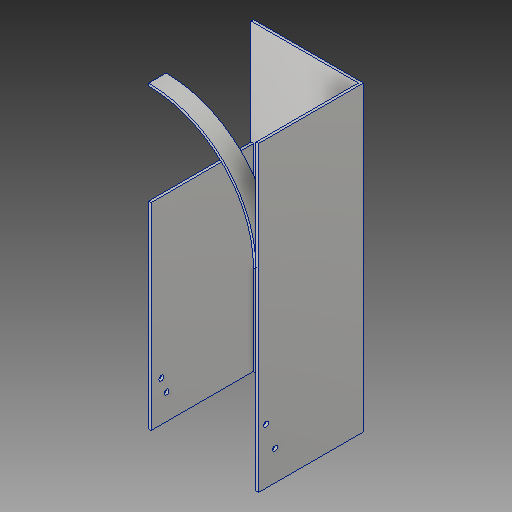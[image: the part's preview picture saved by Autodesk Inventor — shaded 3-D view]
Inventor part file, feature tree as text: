
AUTODESK INVENTOR PART (.ipt)
format: ipt  version: 2019 (Build 230136000, 136)  size: 156,672 bytes
history: native  units: in
note: dims shown in document units (in); Inventor stores cm internally (conversion verified against a paired STEP export)
features: sketch x6, extrude x4, hole x2
ambient origin geometry x8: Origin, YZ Plane, XZ Plane, XY Plane, X Axis, Y Axis, Z Axis, Center Point
bodies: Solid1 (feature_tree)
feature tree (12):
  extrude  "Extrusion1"  Depth=8.646in
  extrude  "Extrusion2"  Depth=0.073in
  extrude  "Extrusion3"  Depth=3.0in
  extrude  "Extrusion7"  Depth=3.0in
  hole  "Hole1"  [1 undecoded]
  hole  "Hole2"  [1 undecoded]
  sketch  "Sketch1"  dims[d0=3.146in d1=8.646in]
  sketch  "Sketch2"  dims[d2=3.0in d3=0.0in d4=0.073in]
  sketch  "Sketch3"  dims[d5=0.073in d6=3.0in]
  sketch  "Sketch9"  dims[d7=9.0in d8=0.0in d9=3.0in]
  sketch  "Sketch10"  dims[d10=2.927in d11=0.0in d22=45.0deg]
  sketch  "Sketch11"  dims[d23=0.073in d24=0.073in d25=0.5in d26=0.0in d27=0.731in d28=0.441in d29=0.289in d30=1.15in d31=0.146in d32=0.38in d33=0.375in d34=0.25in d35=0.5635in d36=0.588in d37=0.8108in d38=1.581in d39=0.213in d40=0.477in d41=0.857in d42=0.146in d43=0.38in d44=0.375in d45=0.25in d46=0.5635in d47=0.588in d48=0.8108in]
note: 2 required parameter values undecoded (feature->parameter linkage not recoverable at this tier; creation-order binding heuristic only, values carry confidence <= 0.55)
